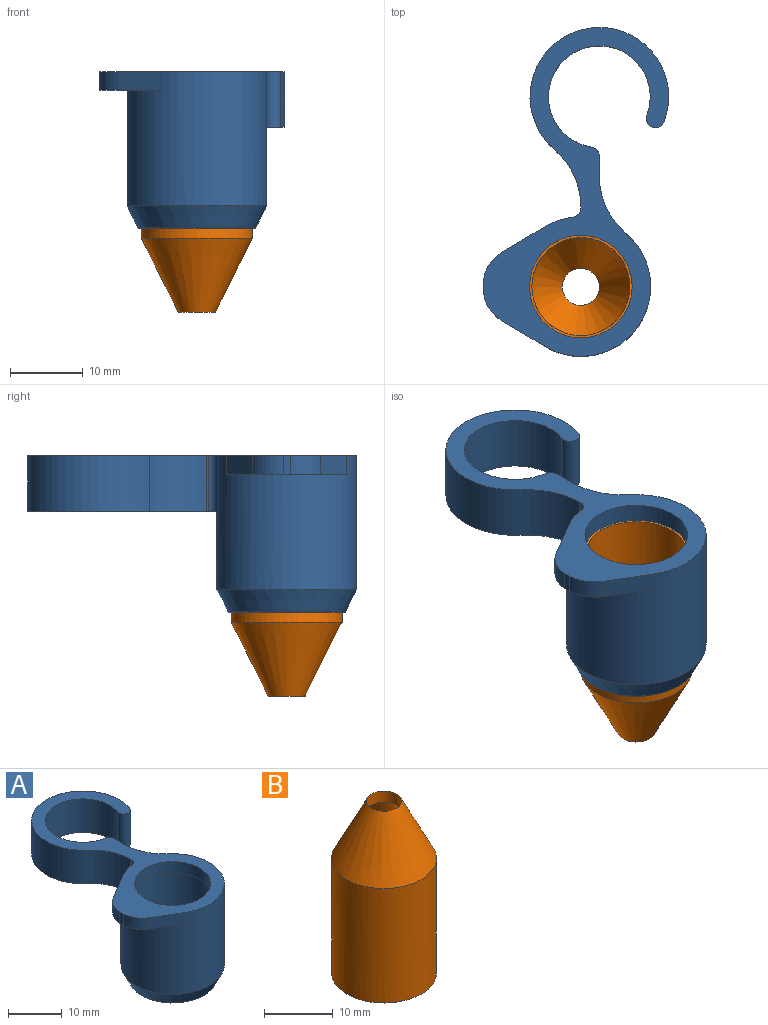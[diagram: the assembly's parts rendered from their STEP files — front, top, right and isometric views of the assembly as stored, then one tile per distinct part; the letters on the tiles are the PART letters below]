
ASSEMBLY  parts=2 mates=2
PART A: 23 faces, bbox 25.5x45.2x21.5 mm
  f0: cylinder r=9.59mm len=19.18mm, axis (0,0,-1), area 999.4mm2, adj f6,f7,f9,f11,f14,f17,f19,f20
  f1: cylinder r=6.99mm len=13.97mm, axis (0,0,-1), area 262.2mm2, adj f6,f7,f10,f12
  f2: cylinder r=9.53mm len=19.05mm, axis (0,0,-1), area 317.9mm2, adj f6,f7,f8,f10
  f3: plane 7.62x0.23mm, normal (-1,0,0), area 1.8mm2, adj f6,f7,f8,f11
  f4: plane 7.62x2.78mm, normal (1,0,0), area 21.2mm2, adj f6,f7,f9,f12
  f5: cylinder r=7.05mm len=14.1mm, axis (0,0,-1), area 112.5mm2, adj f6,f16
  f6: plane 45.17x25.46mm, normal (0,0,1), area 308.9mm2, adj f0,f1,f2,f3,f4,f5,f8,f9
  f7: plane 28.24x19.05mm, normal (0,0,-1), area 136.4mm2, adj f0,f1,f2,f3,f4,f8,f9,f10
  f8: cylinder r=10.16mm len=7.76mm, axis (0,0,-1), area 67.3mm2, adj f2,f3,f6,f7
  f9: cylinder r=10.16mm len=7.78mm, axis (0,0,-1), area 67.5mm2, adj f0,f4,f6,f7
  f10: cylinder r=1.27mm len=7.62mm, axis (0,0,-1), area 30.4mm2, adj f1,f2,f6,f7
  f11: cylinder r=1.27mm len=7.62mm, axis (0,0,-1), area 14.1mm2, adj f0,f3,f6,f7
  f12: cylinder r=1.27mm len=7.62mm, axis (0,0,-1), area 13.7mm2, adj f1,f4,f6,f7
  f13: cylinder r=7.62mm len=18.74mm, axis (0,0,1), area 897mm2, adj f15,f16
  f14: cone r=7.62mm half-angle=26.6deg, axis (0,0,1), area 184.8mm2, adj f0,f15
  f15: torus R=7.87mm, axis (0,0,-1), area 33.5mm2, adj f13,f14
  f16: plane 15.24x15.24mm, normal (0,0,-1), area 26.3mm2, adj f5,f13
  f17: plane 6.01x3.57mm, normal (-0.51,0.86,0), area 17.8mm2, adj f0,f6,f20,f21
  f18: cylinder r=13.4mm len=2.54mm, axis (0,0,1), area 2.5mm2, adj f6,f20,f21,f22
  f19: plane 6.01x3.57mm, normal (-0.51,-0.86,0), area 17.8mm2, adj f0,f6,f20,f22
  f20: plane 16.49x8.5mm, normal (0,0,-1), area 39.8mm2, adj f0,f17,f18,f19,f21,f22
  f21: cylinder r=5.08mm len=4.18mm, axis (0,0,1), area 12.9mm2, adj f6,f17,f18,f20
  f22: cylinder r=5.08mm len=4.18mm, axis (0,0,1), area 12.9mm2, adj f6,f18,f19,f20
PART B: 6 faces, bbox 15.2x15.2x30.5 mm
  f0: cone r=1.74mm half-angle=26.6deg, axis (0,0,-1), area 272.9mm2, adj f4,f5
  f1: cylinder r=7.62mm len=20.32mm, axis (0,0,-1), area 972.9mm2, adj f2,f3
  f2: plane 15.24x15.24mm, normal (0,0,-1), area 40.1mm2, adj f1,f4
  f3: cone r=2.54mm half-angle=26.6deg, axis (0,0,-1), area 362.6mm2, adj f1,f5
  f4: cylinder r=6.73mm len=20.11mm, axis (0,0,-1), area 850.5mm2, adj f0,f2
  f5: cylinder r=2.54mm len=5.08mm, axis (0,0,1), area 31.7mm2, adj f0,f3
PLACE A t=(1.93,1.28,-28.27)mm
PLACE B rot(axis=(1,0,0),180deg) t=(-0.61,-24.77,-23.19)mm
MATE planar B.f1 <-> A.f0  axis (0,0,1) through (-0.61,-24.77,-23.19)mm
MATE cylindrical B.f1 <-> A.f0  axis (0,0,1) through (-0.61,-24.77,-23.19)mm
